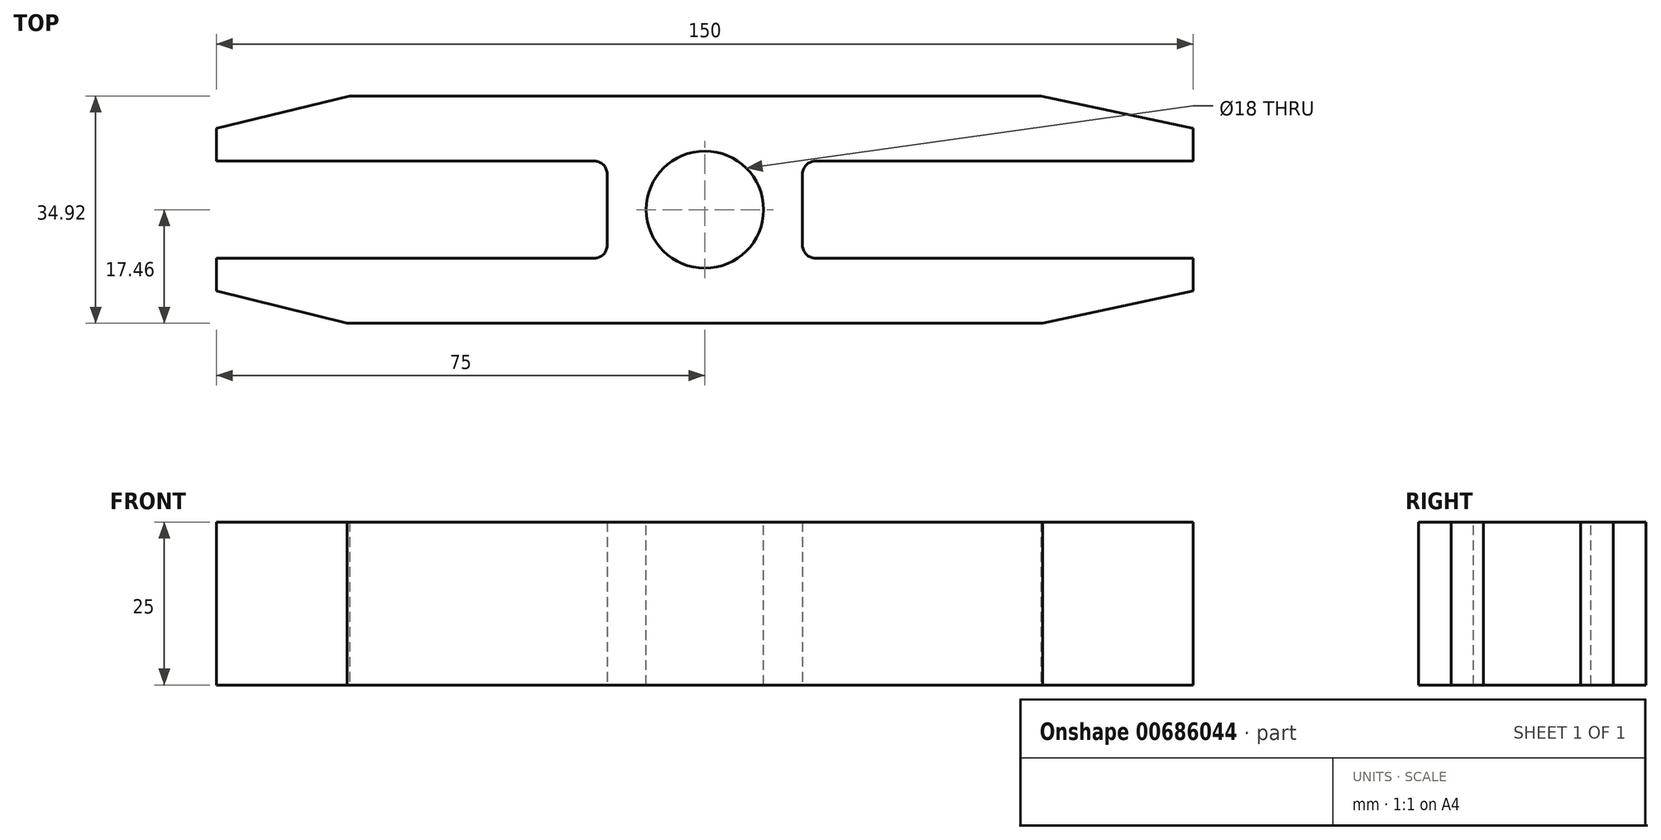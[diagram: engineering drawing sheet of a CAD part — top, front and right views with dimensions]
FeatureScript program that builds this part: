
annotation { "Feature Type Name" : "Feature", "Feature Type Description" : "" }
export const myFeature = defineFeature(function(context is Context, id is Id, definition is map)
    precondition{}
    {
        {
            var Q0;
            Q0=qCreatedBy(makeId("Top.planeOp"),FACE);
            var sketch = newSketch(context, id + "F0", { "sketchPlane" : qUnion([Q0])});
            skLineSegment(sketch, "E0.bottom", {"start": v(75, 75) * mm, "end": v(-75, 75) * mm, "construction": true});
            skLineSegment(sketch, "E0.top", {"start": v(75, -75) * mm, "end": v(-75, -75) * mm, "construction": true});
            skLineSegment(sketch, "E0.left", {"start": v(75, 75) * mm, "end": v(75, -75) * mm, "construction": true});
            skLineSegment(sketch, "E0.right", {"start": v(-75, 75) * mm, "end": v(-75, -75) * mm, "construction": true});
            skPoint(sketch, "E0.middle", {"position": v(0, 0) * mm});
            skLineSegment(sketch, "E1", {"start": v(0, 75) * mm, "end": v(0, -75) * mm, "construction": true});
            skLineSegment(sketch, "E2", {"start": v(-75, 0) * mm, "end": v(75, 0) * mm, "construction": true});
            skLineSegment(sketch, "E3", {"start": v(-75, -7.46) * mm, "end": v(-15, -7.46) * mm});
            skLineSegment(sketch, "E4", {"start": v(-15, -7.46) * mm, "end": v(-15, 7.46) * mm});
            skLineSegment(sketch, "E5", {"start": v(-15, 7.46) * mm, "end": v(-75, 7.46) * mm});
            skLineSegment(sketch, "E6", {"start": v(75, -7.46) * mm, "end": v(15, -7.46) * mm});
            skLineSegment(sketch, "E7", {"start": v(75, 7.46) * mm, "end": v(15, 7.46) * mm});
            skLineSegment(sketch, "E8", {"start": v(15, 7.46) * mm, "end": v(15, -7.46) * mm});
            skLineSegment(sketch, "E9.bottom", {"start": v(-75, 7.46) * mm, "end": v(75, 7.46) * mm, "construction": true});
            skLineSegment(sketch, "E9.top", {"start": v(-75, 17.46) * mm, "end": v(75, 17.46) * mm, "construction": true});
            skLineSegment(sketch, "E9.left", {"start": v(-75, 7.46) * mm, "end": v(-75, 17.46) * mm, "construction": true});
            skLineSegment(sketch, "E9.right", {"start": v(75, 7.46) * mm, "end": v(75, 17.46) * mm, "construction": true});
            skLineSegment(sketch, "E10.bottom", {"start": v(-75, -7.46) * mm, "end": v(75, -7.46) * mm, "construction": true});
            skLineSegment(sketch, "E10.top", {"start": v(-75, -17.46) * mm, "end": v(75, -17.46) * mm, "construction": true});
            skLineSegment(sketch, "E10.left", {"start": v(-75, -7.46) * mm, "end": v(-75, -17.46) * mm, "construction": true});
            skLineSegment(sketch, "E10.right", {"start": v(75, -7.46) * mm, "end": v(75, -17.46) * mm, "construction": true});
            skLineSegment(sketch, "E11", {"start": v(-54.53, 17.46) * mm, "end": v(51.63, 17.46) * mm});
            skLineSegment(sketch, "E12", {"start": v(-54.95, -17.46) * mm, "end": v(51.84, -17.46) * mm});
            skLineSegment(sketch, "E13", {"start": v(51.84, -17.46) * mm, "end": v(75, -12.46) * mm});
            skLineSegment(sketch, "E14", {"start": v(75, -12.46) * mm, "end": v(75, -7.46) * mm});
            skLineSegment(sketch, "E15", {"start": v(-54.53, 17.46) * mm, "end": v(-75, 12.46) * mm});
            skLineSegment(sketch, "E16", {"start": v(-75, 12.46) * mm, "end": v(-75, 7.46) * mm});
            skLineSegment(sketch, "E17", {"start": v(75, 7.46) * mm, "end": v(75, 12.46) * mm});
            skLineSegment(sketch, "E18", {"start": v(75, 12.46) * mm, "end": v(51.63, 17.46) * mm});
            skLineSegment(sketch, "E19", {"start": v(-54.95, -17.46) * mm, "end": v(-75, -12.46) * mm});
            skLineSegment(sketch, "E20", {"start": v(-75, -12.46) * mm, "end": v(-75, -7.46) * mm});
            skSolve(sketch);
        }
        {
            var Q0;
            Q0=makeQuery(id+"F0.imprint","IMPRINT",FACE,{"disambiguationData":[TD([[makeQuery(id+"F0.imprint","IMPRINT",EDGE,{"derivedFrom":sQuery(id+"F0.wireOp",EDGE,"E3")}),-1.0]])]});
            extrude(context, id + "F1", {"entities" : qUnion([Q0]), "depth" : 25 * mm, "offsetDistance" : 25 * mm});
        }
        {
            var Q0;
            Q0=makeQuery(id+"F1.opExtrude","CAP_FACE",FACE,{"disambiguationData":[OSD([sQuery(id+"F0.wireOp",EDGE,"E3"),sQuery(id+"F0.wireOp",EDGE,"E4"),sQuery(id+"F0.wireOp",EDGE,"E5"),sQuery(id+"F0.wireOp",EDGE,"E6"),sQuery(id+"F0.wireOp",EDGE,"E7"),sQuery(id+"F0.wireOp",EDGE,"E8"),sQuery(id+"F0.wireOp",EDGE,"E11"),sQuery(id+"F0.wireOp",EDGE,"E12"),sQuery(id+"F0.wireOp",EDGE,"E13"),sQuery(id+"F0.wireOp",EDGE,"E14"),sQuery(id+"F0.wireOp",EDGE,"E15"),sQuery(id+"F0.wireOp",EDGE,"E16"),sQuery(id+"F0.wireOp",EDGE,"E17"),sQuery(id+"F0.wireOp",EDGE,"E18"),sQuery(id+"F0.wireOp",EDGE,"E19"),sQuery(id+"F0.wireOp",EDGE,"E20")])],"isStart":false});
            var sketch = newSketch(context, id + "F2", { "sketchPlane" : qUnion([Q0])});
            skCircle(sketch, "E21", {"center": v(0, 0) * mm, "radius": 9 * mm});
            skSolve(sketch);
        }
        {
            var Q0;
            Q0=makeQuery(id+"F2.imprint","IMPRINT",FACE,{"disambiguationData":[TD([[makeQuery(id+"F2.imprint","IMPRINT",EDGE,{"derivedFrom":sQuery(id+"F2.wireOp",EDGE,"E21")}),1.0]])]});
            extrude(context, id + "F3", {"entities" : qUnion([Q0]), "operationType" : NewBodyOperationType.REMOVE, "oppositeDirection" : true, "depth" : 40 * mm, "offsetDistance" : 25 * mm});
        }
        {
            var Q0;
            Q0=makeQuery(id+"F1.opExtrude","SWEPT_EDGE",EDGE,{"disambiguationData":[OSD([sQuery(id+"F0.wireOp",EDGE,"E3"),sQuery(id+"F0.wireOp",EDGE,"E4")])]});
            var Q1;
            Q1=makeQuery(id+"F1.opExtrude","SWEPT_EDGE",EDGE,{"disambiguationData":[OSD([sQuery(id+"F0.wireOp",EDGE,"E4"),sQuery(id+"F0.wireOp",EDGE,"E5")])]});
            var Q2;
            Q2=makeQuery(id+"F1.opExtrude","SWEPT_EDGE",EDGE,{"disambiguationData":[OSD([sQuery(id+"F0.wireOp",EDGE,"E6"),sQuery(id+"F0.wireOp",EDGE,"E8")])]});
            var Q3;
            Q3=makeQuery(id+"F1.opExtrude","SWEPT_EDGE",EDGE,{"disambiguationData":[OSD([sQuery(id+"F0.wireOp",EDGE,"E7"),sQuery(id+"F0.wireOp",EDGE,"E8")])]});
            fillet(context, id + "F4", {"entities" : qUnion([Q0, Q1, Q2, Q3]), "radius" : 2 * mm, "tangentPropagation" : true, "allowEdgeOverflow" : false});
        }
    });
